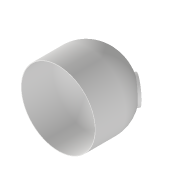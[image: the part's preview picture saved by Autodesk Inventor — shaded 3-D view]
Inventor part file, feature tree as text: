
AUTODESK INVENTOR PART (.ipt)
format: ipt  version: 2020 (Build 240168000, 168)  size: 190,976 bytes
history: native  units: mm
features: sketch x4, extrude x3, revolve x1, projected_geometry x1
ambient origin geometry x8: Origin, YZ Plane, XZ Plane, XY Plane, X Axis, Y Axis, Z Axis, Center Point
bodies: Volumenkörper1 (feature_tree)
feature tree (9):
  revolve  "Umdrehung1"
  extrude  "Extrusion1"  Depth=600.0mm
  extrude  "Extrusion2"  Depth=50.0mm
  extrude  "Extrusion3"  Depth=5.0mm
  sketch  "Skizze1"  dims[d0=0.0mm d1=600.0mm]
  sketch  "Skizze2"  dims[d2=50.0mm d3=500.0mm]
  projected_geometry  "Projizierte Kontur1"
  sketch  "Skizze3"  dims[d4=5.0mm d5=5.0mm]
  sketch  "Skizze4"  dims[d6=50.0mm d7=90.0deg d8=90.0mm d9=10.0mm d10=0.0mm d12=210.0mm d13=27.75mm d14=0.0mm d15=200.0mm d16=0.0mm d17=0.0mm]
